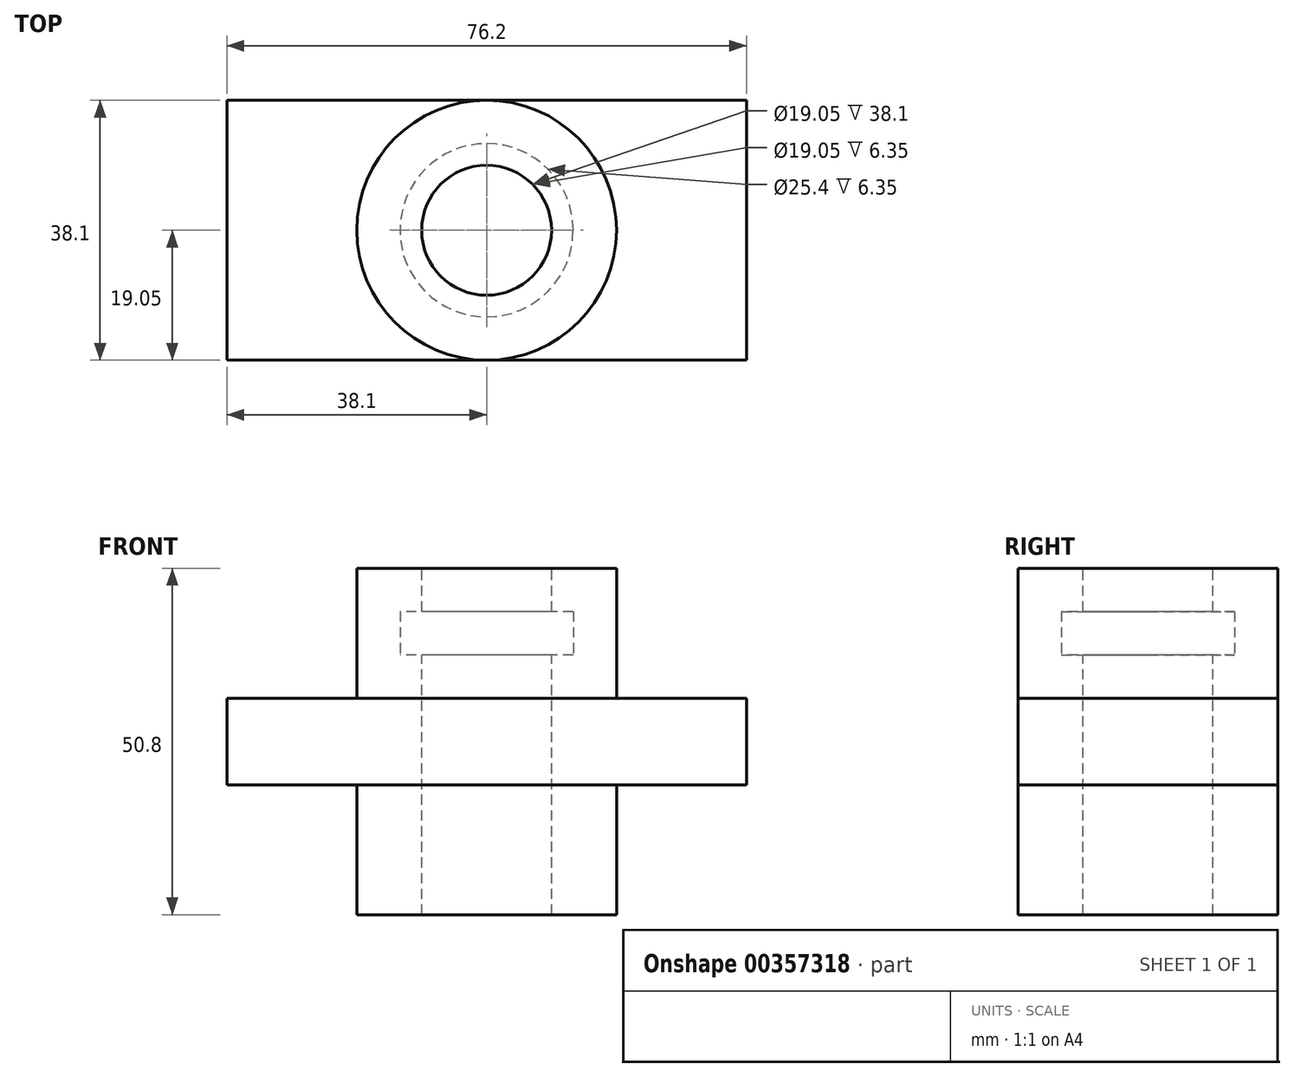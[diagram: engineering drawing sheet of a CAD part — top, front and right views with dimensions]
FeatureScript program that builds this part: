
annotation { "Feature Type Name" : "Feature", "Feature Type Description" : "" }
export const myFeature = defineFeature(function(context is Context, id is Id, definition is map)
    precondition{}
    {
        {
            var Q0;
            Q0=qCreatedBy(makeId("Top.planeOp"),FACE);
            var sketch = newSketch(context, id + "F0", { "sketchPlane" : qUnion([Q0])});
            skLineSegment(sketch, "E0.bottom", {"start": v(-38.1, 19.05) * mm, "end": v(38.1, 19.05) * mm});
            skLineSegment(sketch, "E0.top", {"start": v(-38.1, -19.05) * mm, "end": v(38.1, -19.05) * mm});
            skLineSegment(sketch, "E0.left", {"start": v(-38.1, 19.05) * mm, "end": v(-38.1, -19.05) * mm});
            skLineSegment(sketch, "E0.right", {"start": v(38.1, 19.05) * mm, "end": v(38.1, -19.05) * mm});
            skSolve(sketch);
        }
        {
            var Q0;
            Q0=makeQuery(id+"F0.imprint","IMPRINT",FACE,{"disambiguationData":[TD([[makeQuery(id+"F0.imprint","IMPRINT",EDGE,{"derivedFrom":sQuery(id+"F0.wireOp",EDGE,"E0.bottom")}),-1.0]])]});
            extrude(context, id + "F1", {"entities" : qUnion([Q0]), "endBound" : BoundingType.SYMMETRIC, "depth" : 12.7 * mm});
        }
        {
            var Q0;
            Q0=qCreatedBy(makeId("Top.planeOp"),FACE);
            var sketch = newSketch(context, id + "F2", { "sketchPlane" : qUnion([Q0])});
            skCircle(sketch, "E1", {"center": v(0, 0) * mm, "radius": 19.05 * mm});
            skSolve(sketch);
        }
        {
            var Q0;
            Q0=qSketchRegion(id+"F2",true);
            extrude(context, id + "F3", {"entities" : qUnion([Q0]), "operationType" : NewBodyOperationType.ADD, "endBound" : BoundingType.SYMMETRIC, "depth" : 50.8 * mm});
        }
        {
            var Q0;
            Q0=qCreatedBy(makeId("Top.planeOp"),FACE);
            var sketch = newSketch(context, id + "F4", { "sketchPlane" : qUnion([Q0])});
            skCircle(sketch, "E2", {"center": v(0, 0) * mm, "radius": 9.53 * mm});
            skSolve(sketch);
        }
        {
            var Q0;
            Q0=qSketchRegion(id+"F4",true);
            extrude(context, id + "F5", {"entities" : qUnion([Q0]), "operationType" : NewBodyOperationType.REMOVE, "endBound" : BoundingType.THROUGH_ALL, "oppositeDirection" : true, "depth" : 25.4 * mm, "hasSecondDirection" : true, "secondDirectionBound" : SecondDirectionBoundingType.THROUGH_ALL, "secondDirectionOppositeDirection" : false, "secondDirectionDepth" : 25.4 * mm});
        }
        {
            var Q0;
            Q0=qCreatedBy(makeId("Top.planeOp"),FACE);
            var sketch = newSketch(context, id + "F6", { "sketchPlane" : qUnion([Q0])});
            skCircle(sketch, "E3", {"center": v(0, 0) * mm, "radius": 12.7 * mm});
            skSolve(sketch);
        }
        {
            var Q0;
            Q0=qSketchRegion(id+"F6",true);
            extrude(context, id + "F7", {"entities" : qUnion([Q0]), "operationType" : NewBodyOperationType.REMOVE, "depth" : 19.05 * mm, "hasSecondDirection" : true, "secondDirectionOppositeDirection" : false, "secondDirectionDepth" : 12.7 * mm});
        }
    });
